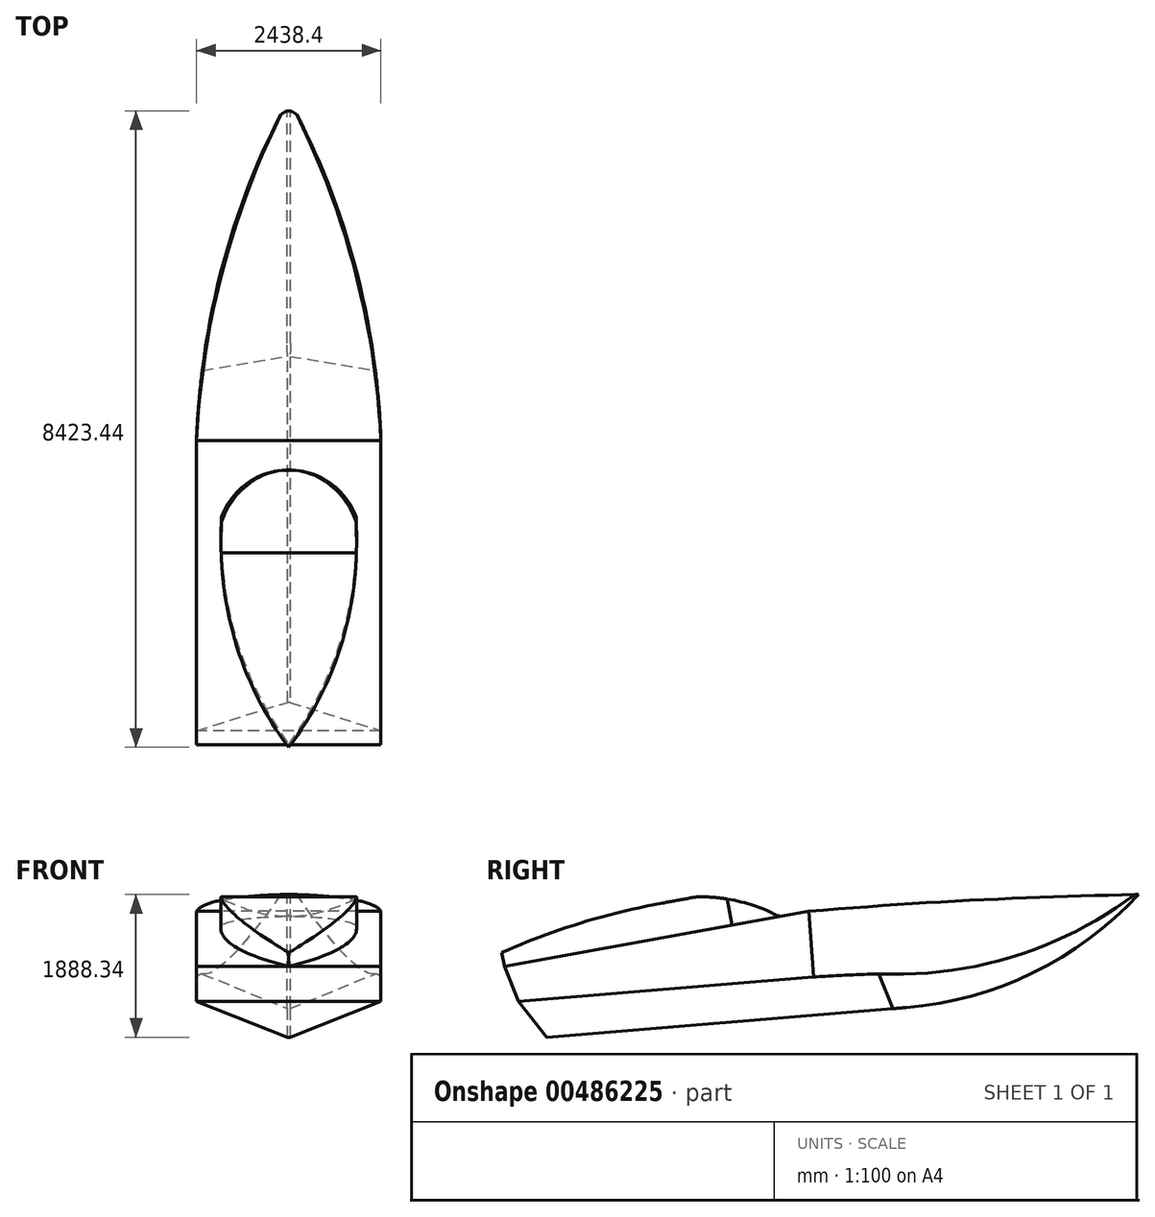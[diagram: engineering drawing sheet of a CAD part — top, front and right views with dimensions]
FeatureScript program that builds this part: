
annotation { "Feature Type Name" : "Feature", "Feature Type Description" : "" }
export const myFeature = defineFeature(function(context is Context, id is Id, definition is map)
    precondition{}
    {
        {
            var Q0;
            Q0=qCreatedBy(makeId("Right.planeOp"),FACE);
            var sketch = newSketch(context, id + "F0", { "sketchPlane" : qUnion([Q0])});
            skLineSegment(sketch, "E0", {"start": v(-4029.59, -665.99) * mm, "end": v(-3844.14, -1124.35) * mm});
            skLineSegment(sketch, "E1", {"start": v(-3844.14, -1124.35) * mm, "end": v(-647.35, -712.7) * mm});
            skArc(sketch, "E2", {"start": v(-647.35, -712.7) * mm, "mid": v(1849.02, -314.26) * mm, "end": v(4316.78, 234.19) * mm});
            skLineSegment(sketch, "E3", {"start": v(-4029.59, -665.99) * mm, "end": v(378, 135.22) * mm});
            skLineSegment(sketch, "E4", {"start": v(4504.81, 451.9) * mm, "end": v(378, 135.22) * mm});
            skLineSegment(sketch, "E5", {"start": v(-3844.14, -1124.35) * mm, "end": v(-4029.59, -665.99) * mm});
            skArc(sketch, "E6", {"start": v(1285.3, -1208.14) * mm, "mid": v(3060.62, -699.2) * mm, "end": v(4504.81, 451.9) * mm});
            skLineSegment(sketch, "E7", {"start": v(-3844.14, -1124.35) * mm, "end": v(-3469.52, -1600.32) * mm});
            skLineSegment(sketch, "E8", {"start": v(-3469.52, -1600.32) * mm, "end": v(1285.3, -1208.14) * mm});
            skSolve(sketch);
        }
        {
            var Q0;
            Q0=makeQuery(id+"F0.imprint","IMPRINT",FACE,{"disambiguationData":[TD([[makeQuery(id+"F0.imprint","IMPRINT",EDGE,{"derivedFrom":sQuery(id+"F0.wireOp",EDGE,"E0")}),1.0]])]});
            var Q1;
            {var subQ4=sQuery(id+"F0.wireOp",EDGE,"E1");Q1=makeQuery(id+"F0.imprint","IMPRINT",FACE,{"disambiguationData":[TD([[makeQuery(id+"F0.imprint","IMPRINT",EDGE,{"derivedFrom":subQ4}),-1.0]])]});}
            extrude(context, id + "F1", {"entities" : qUnion([Q0, Q1]), "depth" : 2438.4 * mm, "offsetDistance" : 25.4 * mm});
        }
        {
            var Q0;
            Q0=makeQuery(id+"F1.opExtrude","SWEPT_FACE",FACE,{"disambiguationData":[OSD([sQuery(id+"F0.wireOp",EDGE,"E0")])]});
            var sketch = newSketch(context, id + "F2", { "sketchPlane" : qUnion([Q0])});
            skLineSegment(sketch, "E9", {"start": v(0, 399.46) * mm, "end": v(1219.2, -136.54) * mm});
            skPoint(sketch, "E9.endSnap0", {"position": v(1219.2, 399.46) * mm});
            skLineSegment(sketch, "E10", {"start": v(1219.2, -136.54) * mm, "end": v(2438.4, 399.46) * mm});
            skLineSegment(sketch, "E11", {"start": v(0, 399.46) * mm, "end": v(-71.08, -501.84) * mm});
            skLineSegment(sketch, "E12", {"start": v(-71.08, -501.84) * mm, "end": v(2438.4, -501.84) * mm});
            skLineSegment(sketch, "E13", {"start": v(2438.4, -501.84) * mm, "end": v(2438.4, 399.46) * mm});
            skSolve(sketch);
        }
        {
            var Q0;
            Q0=makeQuery(id+"F2.imprint","IMPRINT",FACE,{"disambiguationData":[TD([[makeQuery(id+"F2.imprint","IMPRINT",EDGE,{"derivedFrom":sQuery(id+"F2.wireOp",EDGE,"E9")}),-1.0]])]});
            var Q1;
            Q1=makeQuery(id+"F1.opExtrude","CAP_EDGE",EDGE,{"disambiguationData":[OSD([sQuery(id+"F0.wireOp",EDGE,"E8")])],"isStart":true});
            var Q2;
            Q2=makeQuery(id+"F1.opExtrude","CAP_EDGE",EDGE,{"disambiguationData":[OSD([sQuery(id+"F0.wireOp",EDGE,"E6")])],"isStart":true});
            sweep(context, id + "F3", {"operationType" : NewBodyOperationType.REMOVE, "profiles" : qUnion([Q0]), "path" : qUnion([Q1, Q2])});
        }
        {
            var Q0;
            Q0=makeQuery(id+"F1.opExtrude","SWEPT_FACE",FACE,{"disambiguationData":[OSD([sQuery(id+"F0.wireOp",EDGE,"E4")])]});
            var sketch = newSketch(context, id + "F4", { "sketchPlane" : qUnion([Q0])});
            skLineSegment(sketch, "E14", {"start": v(1219.2, 4526.19) * mm, "end": v(1219.2, 387.24) * mm, "construction": true});
            skArc(sketch, "E15", {"start": v(1219.2, 4526.19) * mm, "mid": v(363.13, 2329.48) * mm, "end": v(0, 0) * mm});
            skLineSegment(sketch, "E16", {"start": v(0, 0) * mm, "end": v(-2186.45, 4425.22) * mm});
            skLineSegment(sketch, "E17", {"start": v(-2186.45, 4425.22) * mm, "end": v(534.22, 5322.05) * mm});
            skLineSegment(sketch, "E18", {"start": v(534.22, 5322.05) * mm, "end": v(1219.2, 4526.19) * mm});
            skArc(sketch, "E19.MirrorCS", {"start": v(1219.2, 4526.19) * mm, "mid": v(2075.27, 2329.48) * mm, "end": v(2438.4, 0) * mm});
            skLineSegment(sketch, "E20.MirrorCS", {"start": v(2438.4, 0) * mm, "end": v(4624.85, 4425.22) * mm});
            skLineSegment(sketch, "E21.MirrorCS", {"start": v(4624.85, 4425.22) * mm, "end": v(1904.18, 5322.05) * mm});
            skLineSegment(sketch, "E22.MirrorCS", {"start": v(1904.18, 5322.05) * mm, "end": v(1219.2, 4526.19) * mm});
            skSolve(sketch);
        }
        {
            var Q0;
            Q0 = qSketchRegion(id + "F4", true);
            extrude(context, id + "F5", {"entities" : qUnion([Q0]), "operationType" : NewBodyOperationType.REMOVE, "oppositeDirection" : true, "depth" : 1778 * mm, "offsetDistance" : 25.4 * mm});
        }
        {
            var Q0;
            Q0=makeQuery(id+"F1.opExtrude","SWEPT_FACE",FACE,{"disambiguationData":[OSD([sQuery(id+"F0.wireOp",EDGE,"E3")])]});
            var sketch = newSketch(context, id + "F6", { "sketchPlane" : qUnion([Q0])});
            skLineSegment(sketch, "E23", {"start": v(1219.2, 396.09) * mm, "end": v(24.81, 396.09) * mm, "construction": true});
            skLineSegment(sketch, "E24", {"start": v(24.81, 396.09) * mm, "end": v(0, -4083.73) * mm, "construction": true});
            skLineSegment(sketch, "E25", {"start": v(0, -4083.73) * mm, "end": v(2438.4, -4083.73) * mm, "construction": true});
            skLineSegment(sketch, "E26", {"start": v(2438.4, -4083.73) * mm, "end": v(2413.59, 396.09) * mm, "construction": true});
            skLineSegment(sketch, "E27", {"start": v(2413.59, 396.09) * mm, "end": v(1219.2, 396.09) * mm, "construction": true});
            skLineSegment(sketch, "E28", {"start": v(24.81, 396.09) * mm, "end": v(329.61, 396.09) * mm, "construction": true});
            skLineSegment(sketch, "E29", {"start": v(329.61, 396.09) * mm, "end": v(329.61, -4083.73) * mm, "construction": true});
            skLineSegment(sketch, "E30", {"start": v(1219.2, 396.09) * mm, "end": v(1219.2, -429.17) * mm, "construction": true});
            skLineSegment(sketch, "E31.MirrorCS", {"start": v(2108.79, 396.09) * mm, "end": v(2108.79, -4083.73) * mm, "construction": true});
            skArc(sketch, "E32", {"start": v(329.61, -1023.03) * mm, "mid": v(514.43, -2628.94) * mm, "end": v(1219.2, -4083.73) * mm});
            skArc(sketch, "E33.MirrorCS", {"start": v(2108.79, -1023.03) * mm, "mid": v(1923.97, -2628.94) * mm, "end": v(1219.2, -4083.73) * mm});
            skArc(sketch, "E34", {"start": v(2108.79, -1023.03) * mm, "mid": v(1219.2, -389.34) * mm, "end": v(329.61, -1023.03) * mm});
            skSolve(sketch);
        }
        {
            var Q0;
            Q0 = qSketchRegion(id + "F6", true);
            extrude(context, id + "F7", {"entities" : qUnion([Q0]), "operationType" : NewBodyOperationType.ADD, "depth" : 457.2 * mm, "offsetDistance" : 25.4 * mm});
        }
        {
            var Q0;
            {var subQ0=sQuery(id+"F0.wireOp",EDGE,"E7");var subQ1=sQuery(id+"F0.wireOp",EDGE,"E4");var subQ2=sQuery(id+"F0.wireOp",EDGE,"E3");var subQ4=sQuery(id+"F0.wireOp",EDGE,"E6");var subQ5=sQuery(id+"F0.wireOp",EDGE,"E0");var subQ6=sQuery(id+"F0.wireOp",EDGE,"E8");Q0=makeQuery(id+"F3.boolean.opBoolean","SPLIT",FACE,{"disambiguationData":[TD([makeQuery(id+"F1.opExtrude","SWEPT_FACE",FACE,{"disambiguationData":[OSD([subQ5])]})])],"derivedFrom":makeQuery(id+"F1.opExtrude","CAP_FACE",FACE,{"disambiguationData":[OSD([subQ5,subQ2,subQ1,subQ4,subQ0,subQ6])],"isStart":true})});}
            var sketch = newSketch(context, id + "F8", { "sketchPlane" : qUnion([Q0])});
            skLineSegment(sketch, "E35", {"start": v(4029.59, -665.99) * mm, "end": v(4638.78, 0) * mm});
            skLineSegment(sketch, "E36", {"start": v(4638.78, 0) * mm, "end": v(528.87, 969.93) * mm});
            skLineSegment(sketch, "E37", {"start": v(528.87, 969.93) * mm, "end": v(395.61, -5.4) * mm});
            skArc(sketch, "E38", {"start": v(1490.43, 256.51) * mm, "mid": v(925.73, 197.86) * mm, "end": v(395.61, -5.4) * mm});
            skLineSegment(sketch, "E39", {"start": v(1490.43, 256.51) * mm, "end": v(1940.26, 174.74) * mm});
            skArc(sketch, "E40", {"start": v(4160.67, -522.69) * mm, "mid": v(3072.2, -104.76) * mm, "end": v(1940.26, 174.74) * mm});
            skSolve(sketch);
        }
        {
            var Q0;
            Q0 = qSketchRegion(id + "F8", true);
            extrude(context, id + "F9", {"entities" : qUnion([Q0]), "operationType" : NewBodyOperationType.REMOVE, "oppositeDirection" : true, "depth" : 2540 * mm, "offsetDistance" : 25.4 * mm});
        }
        {
            var Q0;
            {var subQ0=sQuery(id+"F0.wireOp",EDGE,"E7");var subQ1=sQuery(id+"F0.wireOp",EDGE,"E4");var subQ2=sQuery(id+"F0.wireOp",EDGE,"E3");var subQ4=sQuery(id+"F0.wireOp",EDGE,"E6");var subQ5=sQuery(id+"F0.wireOp",EDGE,"E0");var subQ6=sQuery(id+"F0.wireOp",EDGE,"E8");Q0=makeQuery(id+"F3.boolean.opBoolean","SPLIT",FACE,{"disambiguationData":[TD([makeQuery(id+"F1.opExtrude","SWEPT_FACE",FACE,{"disambiguationData":[OSD([subQ5])]})])],"derivedFrom":makeQuery(id+"F1.opExtrude","CAP_FACE",FACE,{"disambiguationData":[OSD([subQ5,subQ2,subQ1,subQ4,subQ0,subQ6])],"isStart":true})});}
            var sketch = newSketch(context, id + "F10", { "sketchPlane" : qUnion([Q0])});
            skArc(sketch, "E41", {"start": v(5.03, 65.6) * mm, "mid": v(-2258.12, 217.64) * mm, "end": v(-4525.2, 290.67) * mm});
            skLineSegment(sketch, "E42", {"start": v(-4525.2, 290.67) * mm, "end": v(-4953.32, 296.99) * mm});
            skLineSegment(sketch, "E43", {"start": v(-4953.32, 296.99) * mm, "end": v(-5028.86, 826.03) * mm});
            skLineSegment(sketch, "E44", {"start": v(5.03, 65.6) * mm, "end": v(5.03, 304.93) * mm});
            skLineSegment(sketch, "E45", {"start": v(5.03, 304.93) * mm, "end": v(-5028.86, 826.03) * mm});
            skSolve(sketch);
        }
        {
            var Q0;
            Q0 = qSketchRegion(id + "F10", true);
            extrude(context, id + "F11", {"entities" : qUnion([Q0]), "operationType" : NewBodyOperationType.REMOVE, "oppositeDirection" : true, "depth" : 3048 * mm, "offsetDistance" : 25.4 * mm});
        }
    });
